# Revit family: Electronics_Loudspeaker_Bose-Professional_Designmax_DM8S
name_source: partatom
category: Communication Devices
revit_build: Autodesk Revit 2017 (Build: 20171027_0315(x64)
units: mm (PartAtom-declared; Revit-internal decimal feet)

## family parameters
Cut with Voids When Loaded = No
Host = Face
Maintain Annotation Orientation = No
OmniClass Number = 23.85.10.11.14.14.14
OmniClass Title = Loudspeakers
Part Type = Normal
Room Calculation Point = No
Round Connector Dimension = Use Diameter
Shared = No

## types (2) — shared parameters
Assembly Code = D5030
Bracket Material = Metal-Bose-Aluminium
Crossover = 1.5 kHz (passive 2-way crossover)
Default Elevation = 1219 mm
Depth = 253 mm
Description = DesignMax loudspeakers bring outstanding audio and aesthetics to any commercial space. With 12 models to choose from, it’s easy to create tailored solutions that deliver instantly impressive sound. QuickHold mounting mechanisms make installation efficient, reducing strain and hassle — and saving substantial time. And with both black and white versions available, DesignMax loudspeakers integrate seamlessly with any décor.

Delivering SPL suitable for foreground music, the 125-watt DesignMax DM8S loudspeaker features a two-way, 8-inch coaxially mounted woofer and a center-firing 1-inch compression driver, producing a 50 Hz - 20 kHz frequency range. The DM8S is surface-mounted and locks onto a hidden QuickHold U-bracket for fast, secure installation. 

FEATURES
Combine models to complete any design, big or small — 12 loudspeakers to mix and match, from 2-inch, low-profile models to 8-inch, high-SPL compression-driver loudspeakers and outdoor-rated options

Deliver instantly impressive sound with custom Bose drivers — no DSP or EQ required. For even better sound, use select Bose DSPs and amplifiers to enable Bose loudspeaker EQ and SmartBass processing, which expands performance and response at any listening level

Blend into any room design with elegant form factors, minimum-bezel grilles available in black or white, and removable logos

Reduce installation time with the patented QuickHold mounting system, which also reduces strain, hassle, and the chance of product damage

Install easily — all models include Euroblock connectors; ceiling-mounted models include plenum-rated backcans, tile-bridges, and front-access audio wiring that makes installation and troubleshooting easier

Deliver high SPL for clear foreground music

Applications
Performing arts venues
Places of worship
Conference centers
Retail stores
Restaurants and bars
Hospitality venues
Edition number = 1
Enviromental = Indoor only
Frequency Range = 52 – 20,000 Hz
Frequency Response = 60 – 20,000 Hz
HF Driver = 1 x 1-inch compression driver, coaxial center-firing (25 mm)
Height = 395 mm
Keynote = 16700
LF Driver = 1 x 8-inch woofer (203 mm)
Manufacturer = Bose Professional
Material = Metal-Bose-Aluminium
Model = DesignMax DM8S
Mounting/Suspension = QuickHold Mounting System with included U-Bracket 4 preset mounting angles: 0°, 15°, 30°, 45° for wall or ceiling placement Two (2) rear M8 screw inserts for use with optional pan & tilt bracket and one (1) rear M8 screw insert
for safety-tether attachment
Nominal Coverage Pattern = 115°  x 115°
Nominal Impedance = 8 Ω (transformer bypass)
Nominal Sensitivity = 90 dB
Operating Temperature Range = 0 to 50 °C (32 °F to 122 °F)
Power Connector = Euroblock 6-pin connector with loop-through, mounted on rear. Accepts 18 AWG  (0.8 mm2) to 14 AWG (2.5 mm2) size wire
Power Handling(Long-term continuous) = 125 W
Power Handling(peak) = 500 W
Product Guid = 1f156eb8-1dee-4ead-8707-320fea076d37
Product data url = https://bimobject.com
Rated Maximum SPL = 117 dB
Transformer Taps Information = 70V: 2.5, 5, 10, 20, 40, 80 W, bypass  100V: 5, 10, 20, 40, 80 W, bypass
URL = https://www.bose.com
Weight = 10.30 kg
Width = 249 mm
Wire/ Conduit Entry = Accepts 18 AWG (0.8 mm2) to 14 AWG (2.5 mm2) size wire

## per-type parameters (varying)
| type | Mesh Material | Product code | Speaker Material |
| DM8S-Black | Grill-Bose-Black | 802080-0110 | Metal-Bose-Black |
| DM8S-White | Grill-Bose-White | 801332-0210 | Metal-Bose-White |

## geometry (parser evidence)
native form markers: Sweep x8
no freeform markers — native parametric forms only
